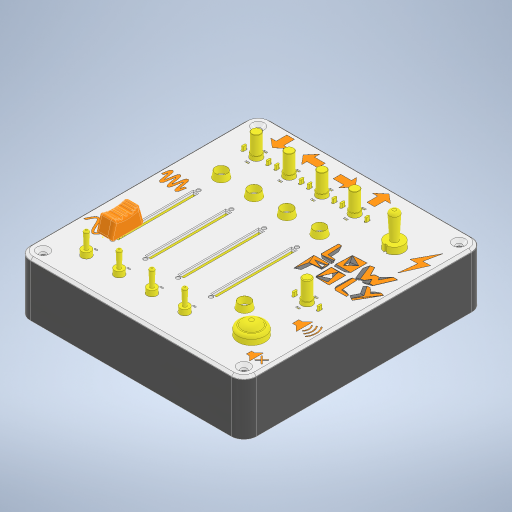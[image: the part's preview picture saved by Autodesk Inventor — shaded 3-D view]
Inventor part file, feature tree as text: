
AUTODESK INVENTOR PART (.ipt)
format: ipt  version: 2024.1 (Build 281209000, 209)  size: 8,110,592 bytes
history: native  units: mm
features: sketch x61, extrude x60, projected_geometry x55, fillet x25, other x13, chamfer x10, plane x2, pattern_linear x2
ambient origin geometry x8: Origin, YZ Plane, XZ Plane, XY Plane, X Axis, Y Axis, Z Axis, Center Point
bodies: Solid12 (feature_tree)
feature tree (228):
  other  "items"
  other  "Blocks"
  extrude  "Extrusion1"  Depth=9.5mm
  extrude  "Extrusion2"  Depth=9.5mm
  extrude  "Extrusion3"  Depth=12.0mm
  extrude  "Extrusion4"  Depth=12.0mm
  extrude  "Extrusion5"  Depth=3.3mm
  extrude  "Extrusion6"  Depth=4.0mm
  extrude  "Extrusion7"  Depth=3.3mm
  extrude  "Extrusion8"  Depth=3.3mm
  extrude  "Extrusion9"  Depth=3.3mm
  extrude  "Extrusion31"  Depth=4.3mm TaperAngle=0.0deg
  fillet  "Fillet1"  Radius=1.76mm
  extrude  "Extrusion10"  Depth=0.57mm
  plane  "Work Plane1"
  extrude  "Extrusion11"  Depth=4.96mm
  extrude  "push-buttons"  Depth=1.22mm
  chamfer  "Chamfer1"  Distance=15.0mm
  extrude  "Extrusion13"  Depth=4.96mm
  fillet  "Fillet3"  Radius=0.49mm
  extrude  "Extrusion14"  Depth=5.0mm TaperAngle=0.0deg
  fillet  "Fillet4"  Radius=1.6mm
  extrude  "toggle-switches"  Depth=56.35mm
  extrude  "Extrusion60"  Depth=5.0mm TaperAngle=0.0deg
  extrude  "Extrusion61"  Depth=15.2mm
  fillet  "Fillet26"  Radius=16.4mm
  extrude  "Extrusion15"  Depth=30.0mm
  extrude  "Extrusion16"  Depth=10.35mm TaperAngle=0.0deg
  extrude  "Extrusion17"  Depth=1.2mm
  extrude  "Extrusion21"  Depth=7.5mm
  extrude  "Extrusion30"  Depth=5.9mm
  fillet  "Fillet5"  Radius=12.0mm
  extrude  "Extrusion18"  Depth=7.65mm
  extrude  "Extrusion19"  Depth=0.74mm
  extrude  "Extrusion20"  Depth=9.1mm
  fillet  "Fillet6"  Radius=4.0mm
  extrude  "Extrusion22"  Depth=20.0mm
  extrude  "faceplate-extrude"  Depth=2.0mm TaperAngle=45.0deg
  fillet  "Fillet7"  Radius=5.48mm
  extrude  "Extrusion24"  Depth=3.0mm TaperAngle=0.0deg
  chamfer  "Chamfer2"  Distance=11.1mm
  chamfer  "Chamfer3"  Distance=12.3mm
  sketch  "Sketch25"  dims[d64=0.5mm d65=7.65mm]
  extrude  "knob-extrude"  Depth=6.8mm
  extrude  "Extrusion26"  Depth=5.9mm
  extrude  "Extrusion27"  Depth=10.0mm TaperAngle=0.0deg
  chamfer  "Chamfer4"  Distance=6.2mm
  chamfer  "Chamfer5"  Distance=28.0mm
  extrude  "Extrusion28"  Depth=17.15mm
  fillet  "Fillet8"  Radius=2.0mm
  chamfer  "Chamfer6"  Distance=1.2mm
  fillet  "Fillet9"  Radius=1.2mm
  extrude  "Extrusion29"  Depth=0.2mm
  fillet  "Fillet10"  Radius=7.5mm
  chamfer  "Chamfer7"  Distance=7.5mm
  fillet  "Fillet11"  Radius=7.5mm
  chamfer  "Chamfer8"  Distance=7.5mm
  chamfer  "Chamfer9"  Distance=7.5mm
  extrude  "Extrusion32"  Depth=0.2mm TaperAngle=0.0deg
  extrude  "Extrusion33"  Depth=0.2mm
  fillet  "Fillet12"  Radius=5.2mm
  chamfer  "Chamfer10"  Distance=0.85mm
  extrude  "Extrusion34"  Depth=0.2mm TaperAngle=0.0deg
  extrude  "bracing"  Depth=0.2mm
  extrude  "graphics-controls"  Depth=0.2mm
  fillet  "Fillet13"  Radius=0.8mm
  fillet  "Fillet14"  Radius=0.1mm
  extrude  "waves"  Depth=0.2mm
  fillet  "Fillet15"  Radius=0.2mm
  fillet  "Fillet16"  Radius=0.3mm
  extrude  "logo"  Depth=0.2mm
  fillet  "Fillet17"  Radius=2.0mm
  extrude  "Extrusion41"  Depth=0.2mm
  extrude  "Extrusion42"  Depth=0.2mm
  extrude  "Extrusion43"  Depth=0.2mm
  extrude  "Extrusion44"  TaperAngle=0.0deg  [1 undecoded]
  fillet  "Fillet18"  Radius=2.0mm
  fillet  "Fillet19"  Radius=0.2mm
  fillet  "Fillet21"  Radius=10.0mm
  extrude  "Extrusion45"  Depth=0.2mm
  extrude  "Extrusion46"  Depth=0.2mm
  extrude  "Extrusion47"  Depth=0.2mm
  fillet  "Fillet20"  Radius=3.98mm
  extrude  "Extrusion48"  Depth=0.2mm
  fillet  "Fillet22"  Radius=10.0mm
  fillet  "Fillet23"  Radius=6.5mm
  plane  "Work Plane2"
  extrude  "Extrusion49"  Depth=0.2mm TaperAngle=0.0deg
  pattern_linear  "Rectangular Pattern1"  Spacing1=4.0mm  [1 undecoded]
  extrude  "Extrusion50"  Depth=0.2mm TaperAngle=45.0deg
  extrude  "Extrusion51"  TaperAngle=0.0deg  [1 undecoded]
  fillet  "Fillet24"  Radius=1.0mm
  extrude  "6.35-jack-hole"  Depth=0.2mm TaperAngle=45.0deg
  extrude  "Extrusion53"  Depth=0.2mm
  extrude  "Extrusion54"  Depth=0.2mm
  extrude  "Extrusion55"  Depth=0.2mm
  fillet  "Fillet25"  Radius=1.8mm
  extrude  "Extrusion56"  Depth=0.2mm
  extrude  "Extrusion57"  Depth=0.2mm
  extrude  "Extrusion58"  Depth=0.2mm
  pattern_linear  "Rectangular Pattern2"  Spacing1=1.0mm  [1 undecoded]
  extrude  "Extrusion62"  TaperAngle=0.0deg  [1 undecoded]
  sketch  "Sketch1"  dims[d0=60.0mm d1=9.5mm]
  sketch  "Sketch2"  dims[d2=9.5mm d3=9.5mm]
  sketch  "Sketch3"  dims[d4=9.5mm d5=12.0mm]
  sketch  "Sketch4"  dims[d6=12.0mm d7=12.0mm]
  projected_geometry  "Projected Loop1"
  sketch  "Sketch5"  dims[d8=6.0mm d9=0.0mm d10=3.3mm]
  projected_geometry  "Projected Loop2"
  projected_geometry  "Projected Loop3"
  projected_geometry  "Projected Loop4"
  sketch  "Sketch6"  dims[d11=3.3mm d12=4.0mm]
  sketch  "Sketch7"  dims[d13=4.0mm d14=3.3mm]
  sketch  "Sketch8"  dims[d15=3.3mm d16=3.3mm]
  sketch  "Sketch9"  dims[d17=3.3mm d18=3.3mm]
  projected_geometry  "Projected Loop5"
  sketch  "Sketch10"  dims[d19=3.3mm d20=4.3mm d21=0.0mm d22=1.76mm]
  projected_geometry  "Projected Loop6"
  sketch  "Sketch11"  dims[d24=2.9mm d25=0.57mm]
  projected_geometry  "Projected Loop7"
  sketch  "Sketch12"  dims[d26=1.97mm d27=4.96mm]
  sketch  "Sketch13"  dims[d28=1.495mm d29=1.22mm]
  sketch  "Sketch14"  dims[d30=0.27mm d31=15.0mm d32=0.0mm]
  sketch  "Sketch15"  dims[d33=3.98mm d34=4.96mm d35=0.49mm]
  sketch  "Sketch16"  dims[d36=5.0mm d37=0.0mm d38=5.0mm d39=0.0mm d40=1.6mm]
  sketch  "Sketch17"  dims[d41=1.825mm d42=56.35mm]
  projected_geometry  "Projected Loop8"
  sketch  "Sketch18"  dims[d43=1.825mm d44=5.0mm d45=0.0mm]
  sketch  "Sketch19"  dims[d46=19.0mm d47=15.2mm d48=16.4mm]
  projected_geometry  "Projected Loop9"
  sketch  "Sketch20"  dims[d49=30.0mm d50=30.0mm]
  projected_geometry  "Projected Loop10"
  sketch  "Sketch21"  dims[d51=30.0mm d53=10.35mm d54=0.0mm]
  projected_geometry  "Projected Loop11"
  projected_geometry  "Projected Loop12"
  projected_geometry  "Projected Loop13"
  projected_geometry  "Projected Loop14"
  projected_geometry  "Projected Loop15"
  projected_geometry  "Projected Loop20"
  projected_geometry  "Projected Loop21"
  sketch  "Sketch22"  dims[d55=6.8mm d56=1.2mm]
  projected_geometry  "Projected Loop22"
  projected_geometry  "Projected Loop23"
  projected_geometry  "Projected Loop24"
  projected_geometry  "Projected Loop25"
  projected_geometry  "Projected Loop26"
  sketch  "Sketch23"  dims[d57=2.87mm d58=7.5mm]
  other  "faceplate"
  sketch  "Sketch24"  dims[d59=4.5mm d60=0.0mm d61=5.9mm d62=12.0mm d63=0.0mm]
  sketch  "Sketch26"  dims[d67=13.0mm d68=0.74mm]
  projected_geometry  "Projected Loop27"
  other  "slider-knob"
  sketch  "Sketch27"  dims[d69=9.2mm d70=0.0mm d71=9.1mm d72=4.0mm d73=-1.745329mm]
  projected_geometry  "Projected Loop28"
  sketch  "Sketch28"  dims[d74=2.0mm d77=20.0mm]
  projected_geometry  "Projected Loop29"
  sketch  "Sketch29"  dims[d78=12.3mm d79=0.0mm d80=2.0mm d81=2.0mm d82=45.0deg d84=5.48mm d85=0.0mm]
  projected_geometry  "Projected Loop30"
  sketch  "Sketch30"  dims[d87=2.0mm d89=3.0mm d90=0.0mm]
  sketch  "Sketch31"  dims[d91=5.0mm d92=11.1mm d93=5.55mm]
  sketch  "Sketch32"  dims[d94=11.1mm]
  projected_geometry  "Projected Loop31"
  projected_geometry  "Projected Loop32"
  projected_geometry  "Projected Loop33"
  projected_geometry  "Projected Loop34"
  projected_geometry  "Projected Loop35"
  projected_geometry  "Projected Loop36"
  projected_geometry  "Projected Loop37"
  projected_geometry  "Projected Loop38"
  projected_geometry  "Projected Loop39"
  projected_geometry  "Projected Loop40"
  projected_geometry  "Projected Loop41"
  projected_geometry  "Projected Loop42"
  projected_geometry  "Projected Loop43"
  projected_geometry  "Projected Loop45"
  sketch  "Sketch33"  dims[d95=5.55mm]
  sketch  "Sketch34"  dims[d96=11.1mm]
  sketch  "Sketch35"  dims[d98=11.1mm]
  projected_geometry  "Projected Loop46"
  projected_geometry  "Projected Loop47"
  projected_geometry  "Projected Loop48"
  projected_geometry  "Projected Loop49"
  projected_geometry  "Projected Loop50"
  projected_geometry  "Projected Loop51"
  projected_geometry  "Projected Loop52"
  projected_geometry  "Projected Loop53"
  projected_geometry  "Projected Loop54"
  projected_geometry  "Projected Loop55"
  projected_geometry  "Projected Loop56"
  sketch  "Sketch36"  dims[d99=5.55mm]
  sketch  "Sketch38"  dims[d100=11.1mm]
  other  "2D Equation Curve1"
  sketch  "Sketch40"  dims[d101=5.55mm]
  other  "2D Equation Curve2"
  other  "2D Equation Curve4"
  other  "low-poly-logo"
  sketch  "Sketch42"  dims[d102=10.7mm]
  other  "000-low-poly-logo"
  sketch  "Sketch43"  dims[d103=10.7mm]
  projected_geometry  "Projected Loop57"
  other  "case-body"
  sketch  "Sketch44"  dims[d104=15.2mm]
  projected_geometry  "Projected Loop58"
  sketch  "Sketch45"  dims[d105=15.2mm]
  projected_geometry  "Projected Loop59"
  projected_geometry  "Projected Loop60"
  sketch  "Sketch46"  dims[d108=23.0mm]
  sketch  "Sketch47"  dims[d109=17.0mm d110=12.3mm d111=0.0mm]
  other  "circuit-boards"
  sketch  "Sketch48"  dims[d112=6.8mm d113=6.8mm]
  sketch  "Sketch49"  dims[d114=10.0mm d115=0.0mm d116=5.9mm]
  sketch  "Sketch50"  dims[d117=5.9mm d118=10.0mm d119=0.0mm]
  sketch  "Sketch51"  dims[d120=0.2mm]
  sketch  "Sketch52"  dims[d121=11.9mm d122=6.2mm d123=0.0mm]
  sketch  "Sketch53"  dims[d124=16.0mm]
  sketch  "Sketch54"  dims[d125=29.0mm]
  sketch  "Sketch55"  dims[d126=14.5mm]
  other  "jacks"
  sketch  "Sketch56"  dims[d127=8.0mm d128=28.0mm d129=0.0mm]
  sketch  "Sketch57"  dims[d130=4.8mm d131=17.15mm d132=0.523599mm d133=2.0mm]
  sketch  "Sketch58"  dims[d134=20.0mm]
  sketch  "Sketch59"  dims[d135=26.0mm]
  sketch  "Sketch60"  dims[d136=16.0mm]
  sketch  "Sketch61"  dims[d138=1.2mm]
  sketch  "Sketch62"  dims[d139=2.87mm]
  sketch  "Sketch63"  dims[d140=1.2mm]
  sketch  "Sketch64"  dims[d141=1.2mm d142=1.2mm d143=1.2mm d144=2.87mm d145=7.5mm d146=7.5mm d147=7.5mm d148=7.5mm d149=7.5mm d150=17.15mm d151=0.0mm d152=1.7mm d153=5.2mm d154=0.85mm d155=10.0mm d156=0.0mm d158=0.2mm d159=0.2mm d160=0.8mm d161=0.1mm d162=0.1mm d163=0.2mm d164=0.3mm d165=0.25mm d167=2.0mm d168=0.0mm d169=0.2mm d170=8.0mm d171=4.0mm d172=0.0mm d173=0.0mm d174=2.0mm d175=2.0mm d176=45.0deg d177=0.2mm d178=2.0mm d179=45.0deg d180=10.0mm d181=22.0mm d182=1.76mm d183=4.12mm d184=3.98mm d185=9.01mm d186=10.0mm d187=0.0mm d188=6.5mm d189=0.0mm d190=2.5mm d191=0.0mm d192=4.0mm d193=2.0mm d194=45.0deg d195=2.5mm d196=9.0mm d197=45.0deg d198=0.0mm d199=0.0mm d200=1.0mm d201=2.5mm d202=9.0mm d203=45.0deg d204=2.0mm d205=0.9mm d206=1.2mm d207=1.8mm d208=1.3mm d209=2.0mm d210=1.5mm d211=1.0mm d212=0.0mm d213=0.0mm d214=0.4mm d215=3.341737mm d216=2.5mm d217=9.0mm d218=45.0deg d219=0.5mm d221=7.5mm d222=7.5mm d223=7.5mm d224=7.5mm d225=1.2mm d226=1.2mm d227=1.2mm d228=1.2mm d229=5.5mm d230=1.9mm d231=0.77mm d232=1.9mm d233=0.77mm d234=1.9mm d235=0.77mm d236=1.9mm d237=0.77mm d238=1.9mm d239=0.77mm d240=1.9mm d241=0.77mm d242=1.9mm d243=0.77mm d244=1.9mm d245=0.77mm d246=5.5mm d247=1.4mm d248=0.0mm d249=1.2mm d253=1.2mm d255=7.5mm d256=2.87mm d257=1.9mm d258=0.77mm d259=1.9mm d260=0.77mm d261=11.0mm d262=5.5mm d263=1.4mm d264=0.0mm d265=0.2mm d266=0.5mm d267=2.0mm d268=45.0deg d269=1.5mm d270=2.0mm d271=45.0deg d273=1.5mm d274=0.5mm d275=0.0mm d276=25.0mm d277=0.4mm d278=0.0mm d279=2.0mm d280=0.4mm d281=2.0mm d282=45.0deg d283=12.0mm d284=1.5mm d285=0.0mm d286=1.5mm d287=0.0mm d304=7.0mm d314=5.0mm d315=5.0mm d316=12.0mm d317=2.0mm d318=12.0mm d319=7.0mm d320=7.0mm d321=5.0mm d322=5.0mm d323=5.0mm d324=5.0mm d325=7.0mm d326=5.0mm d327=5.0mm d328=12.0mm d329=12.0mm d330=3.0mm d331=4.2mm d332=3.36mm d333=2.52mm d334=3.36mm d335=10.92mm d336=0.672mm d337=2.94mm d338=2.94mm d339=4.116mm d340=4.116mm d341=5.208mm d342=0.672mm d343=0.672mm d344=1.68mm d345=1.68mm d346=1.68mm d347=3.36mm d348=2.94mm d349=2.1mm d350=2.94mm d351=13.0mm d363=45.0deg d364=90.0deg d365=3.36mm d366=0.756mm d367=0.756mm d368=2.1mm d369=2.1mm d370=0.0mm d371=10.0mm d372=0.05mm d373=0.0mm d374=0.1mm d375=0.05mm d376=0.0mm d377=10.0mm d380=0.0mm d381=3600.0mm d390=0.0mm d391=10800.0mm d394=0.0mm d395=10800.0mm d396=1.5mm d397=1.0mm d398=3.0mm d400=0.0mm d401=3600.0mm d402=1.5mm d403=3.0mm d404=1.0mm d405=0.05mm d406=0.0mm d407=1.0mm d408=0.15mm d422=5.208mm d426=0.05mm d427=0.0mm d428=60.0mm d429=32.0mm d430=0.1mm d431=0.1mm d432=0.1mm d435=0.1mm d437=30.0mm d438=0.0mm d439=0.4mm d440=2.0mm d441=2.0mm d442=0.0mm d443=2.0mm d444=0.0mm d445=43.0mm d446=55.0mm d447=3.0mm d448=3.0mm d449=6.0mm d450=0.0mm d451=2.0mm d452=5.0mm d453=43.0mm d454=55.0mm d455=3.0mm d456=3.0mm d457=3.0mm d458=4.0mm d459=0.0mm d460=10.1mm d461=19.1mm d462=11.2mm d463=23.0mm d464=7.0mm d465=0.0mm d466=16.4mm d469=32.0mm d470=0.0mm d471=1.0mm d473=4.12mm d474=5.5mm d475=1.0mm d476=0.5mm d477=3.2mm d478=5.0mm d479=3.0mm d481=5.0mm d482=5.0mm d483=5.0mm d484=3.0mm d485=4.0mm d486=4.0mm d487=5.0mm d488=8.0mm d489=44.0mm d490=0.0mm d491=0.0mm d492=260.0mm d493=3.0mm d494=30.0mm d495=11.5mm d496=11.5mm d497=3.0mm d498=0.0mm d499=30.0mm d501=11.0mm d502=5.0mm d503=4.0mm d504=6.0mm d505=0.0mm d506=4.999995mm d507=5.0mm d508=1.5mm d509=1.499992mm d510=3.0mm d511=1.5mm d512=5.0mm d513=6.0mm d514=28.0mm d515=0.0mm d516=0.0mm d517=200.0mm d518=11.0mm d519=20.0mm d520=8.0mm d521=22.0mm d522=6.0mm d523=0.0mm d524=10.83mm d525=8.5mm d526=0.0mm d527=6.5mm d528=20.1mm d529=10.05mm d530=7.9mm d531=14.8mm d532=26.0mm d533=0.0mm d534=0.4mm d535=0.4mm d536=1.3mm d537=1.3mm d538=1.3mm d539=3.4mm d540=2.0mm d541=2.0mm d542=5.05mm d543=5.05mm d544=4.5mm d545=0.0mm d546=0.6mm d547=24.0mm d548=14.0mm d549=11.5mm d550=0.0mm d551=0.0mm d552=18.0mm d553=22.0mm d554=0.0mm d556=3.0mm d557=22.0mm d558=0.0mm d559=20.0mm d561=131.6mm d562=20.0mm d564=141.0mm d565=12.06mm d566=7.06mm d567=12.77mm d568=9.0mm d569=7.06mm d570=12.77mm d571=7.06mm d572=12.77mm d573=7.06mm d574=12.77mm d575=13.05mm d576=0.0mm d577=6.1mm d578=5.5mm d579=0.0mm d580=2.5mm d581=10.8mm d582=0.349066mm d583=1.0mm d584=18.35mm d585=35.0mm d586=0.15mm d587=8.4mm d588=8.4mm d589=2.2mm d590=0.9mm d591=6.3mm d592=0.0mm d593=0.0mm]
  other  "000-low-poly-logo:1"
note: 5 required parameter values undecoded (feature->parameter linkage not recoverable at this tier; creation-order binding heuristic only, values carry confidence <= 0.55)
